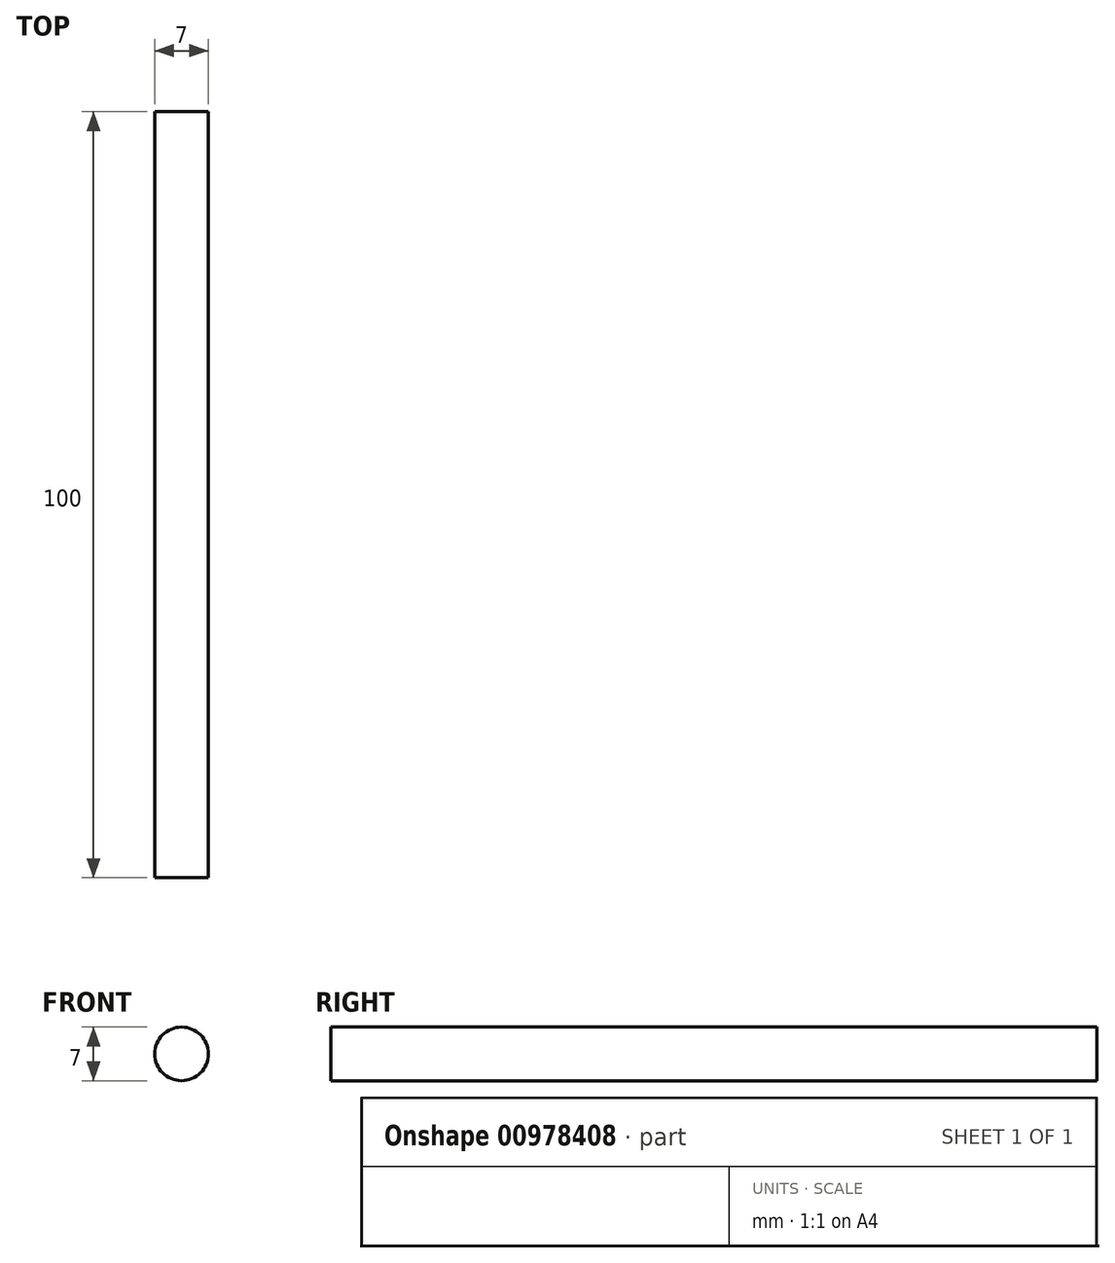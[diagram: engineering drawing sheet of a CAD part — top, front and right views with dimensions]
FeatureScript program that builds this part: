
annotation { "Feature Type Name" : "Feature", "Feature Type Description" : "" }
export const myFeature = defineFeature(function(context is Context, id is Id, definition is map)
    precondition{}
    {
        {
            var Q0;
            Q0=qCreatedBy(makeId("Front.planeOp"),FACE);
            var sketch = newSketch(context, id + "F0", { "sketchPlane" : qUnion([Q0])});
            skCircle(sketch, "E0", {"center": v(0, 0) * mm, "radius": 3.5 * mm});
            skSolve(sketch);
        }
        {
            var Q0;
            Q0 = qSketchRegion(id + "F0", true);
            extrude(context, id + "F1", {"entities" : qUnion([Q0]), "endBound" : BoundingType.SYMMETRIC, "depth" : 100 * mm, "offsetDistance" : 25 * mm});
        }
    });
